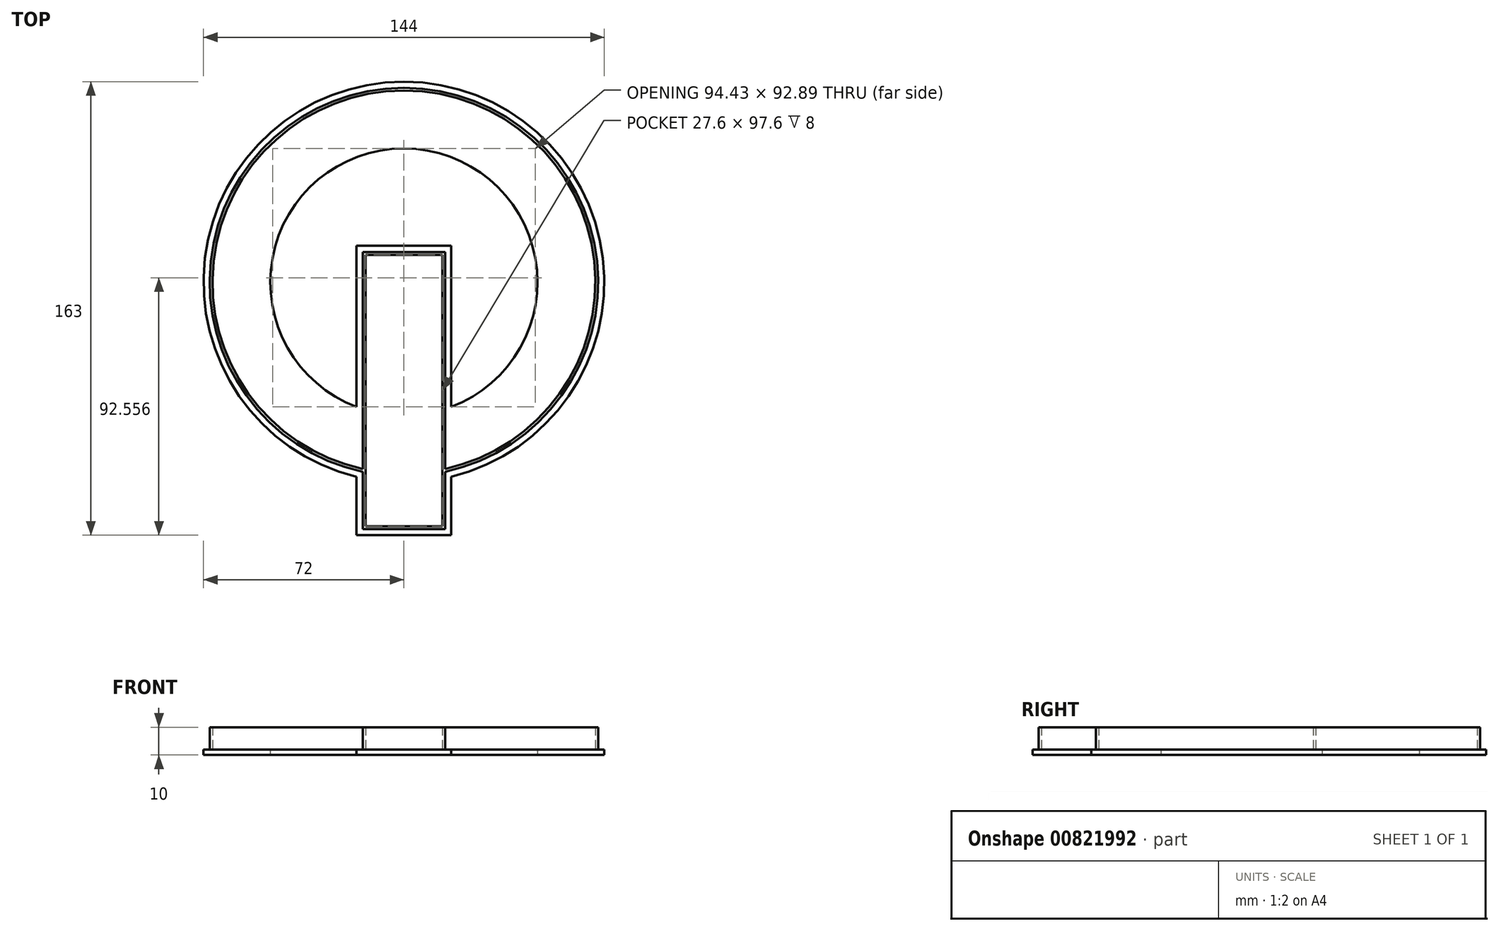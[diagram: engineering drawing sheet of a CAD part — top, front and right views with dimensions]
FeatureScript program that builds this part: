
annotation { "Feature Type Name" : "Feature", "Feature Type Description" : "" }
export const myFeature = defineFeature(function(context is Context, id is Id, definition is map)
    precondition{}
    {
        {
            var Q0;
            Q0=qCreatedBy(makeId("Top.planeOp"),FACE);
            var sketch = newSketch(context, id + "F0", { "sketchPlane" : qUnion([Q0])});
            skCircle(sketch, "E0", {"center": v(0, 0) * mm, "radius": 69.8 * mm});
            skCircle(sketch, "E1", {"center": v(0, 0) * mm, "radius": 68.8 * mm});
            skSolve(sketch);
        }
        {
            var Q0;
            Q0=makeQuery(id+"F0.imprint","IMPRINT",FACE,{"disambiguationData":[TD([[makeQuery(id+"F0.imprint","IMPRINT",EDGE,{"derivedFrom":sQuery(id+"F0.wireOp",EDGE,"E0")}),1.0]])]});
            extrude(context, id + "F1", {"entities" : qUnion([Q0]), "depth" : 10 * mm, "offsetDistance" : 25 * mm});
        }
        {
            var Q0;
            Q0=qCreatedBy(makeId("Top.planeOp"),FACE);
            var sketch = newSketch(context, id + "F2", { "sketchPlane" : qUnion([Q0])});
            skLineSegment(sketch, "E2.bottom", {"start": v(-14.8, 10.8) * mm, "end": v(14.8, 10.8) * mm});
            skLineSegment(sketch, "E2.top", {"start": v(-14.8, -88.8) * mm, "end": v(14.8, -88.8) * mm});
            skLineSegment(sketch, "E2.left", {"start": v(-14.8, 10.8) * mm, "end": v(-14.8, -88.8) * mm});
            skLineSegment(sketch, "E2.right", {"start": v(14.8, 10.8) * mm, "end": v(14.8, -88.8) * mm});
            skPoint(sketch, "E2.middle", {"position": v(0, -39) * mm});
            skLineSegment(sketch, "E3.bottom", {"start": v(-13.8, 9.8) * mm, "end": v(13.8, 9.8) * mm});
            skLineSegment(sketch, "E3.top", {"start": v(-13.8, -87.8) * mm, "end": v(13.8, -87.8) * mm});
            skLineSegment(sketch, "E3.left", {"start": v(-13.8, 9.8) * mm, "end": v(-13.8, -87.8) * mm});
            skLineSegment(sketch, "E3.right", {"start": v(13.8, 9.8) * mm, "end": v(13.8, -87.8) * mm});
            skSolve(sketch);
        }
        {
            var Q0;
            Q0=makeQuery(id+"F2.imprint","IMPRINT",FACE,{"disambiguationData":[TD([[makeQuery(id+"F2.imprint","IMPRINT",EDGE,{"derivedFrom":sQuery(id+"F2.wireOp",EDGE,"E2.bottom")}),-1.0]])]});
            extrude(context, id + "F3", {"entities" : qUnion([Q0]), "operationType" : NewBodyOperationType.ADD, "depth" : 10 * mm, "offsetDistance" : 25 * mm});
        }
        {
            var Q0;
            Q0=qCreatedBy(makeId("Top.planeOp"),FACE);
            var sketch = newSketch(context, id + "F4", { "sketchPlane" : qUnion([Q0])});
            skCircle(sketch, "E4", {"center": v(0, 0) * mm, "radius": 48 * mm});
            skCircle(sketch, "E5", {"center": v(0, 0) * mm, "radius": 68.8 * mm});
            skSolve(sketch);
        }
        {
            var Q0;
            Q0=makeQuery(id+"F4.imprint","IMPRINT",FACE,{"disambiguationData":[TD([[makeQuery(id+"F4.imprint","IMPRINT",EDGE,{"derivedFrom":sQuery(id+"F4.wireOp",EDGE,"E4")}),-1.0]])]});
            extrude(context, id + "F5", {"entities" : qUnion([Q0]), "operationType" : NewBodyOperationType.ADD, "depth" : 2 * mm, "offsetDistance" : 25 * mm});
        }
        {
            var Q0;
            Q0=qCreatedBy(makeId("Top.planeOp"),FACE);
            var sketch = newSketch(context, id + "F6", { "sketchPlane" : qUnion([Q0])});
            skCircle(sketch, "E6", {"center": v(0, 0) * mm, "radius": 69.8 * mm});
            skCircle(sketch, "E7", {"center": v(0, 0) * mm, "radius": 72 * mm});
            skSolve(sketch);
        }
        {
            var Q0;
            Q0=makeQuery(id+"F6.imprint","IMPRINT",FACE,{"disambiguationData":[TD([[makeQuery(id+"F6.imprint","IMPRINT",EDGE,{"derivedFrom":sQuery(id+"F6.wireOp",EDGE,"E6")}),-1.0]])]});
            extrude(context, id + "F7", {"entities" : qUnion([Q0]), "operationType" : NewBodyOperationType.ADD, "depth" : 2 * mm, "offsetDistance" : 25 * mm});
        }
        {
            var Q0;
            Q0=qCreatedBy(makeId("Top.planeOp"),FACE);
            var sketch = newSketch(context, id + "F8", { "sketchPlane" : qUnion([Q0])});
            skLineSegment(sketch, "E8.bottom", {"start": v(-14.8, 10.8) * mm, "end": v(14.8, 10.8) * mm});
            skLineSegment(sketch, "E8.top", {"start": v(-14.8, -88.8) * mm, "end": v(14.8, -88.8) * mm});
            skLineSegment(sketch, "E8.left", {"start": v(-14.8, 10.8) * mm, "end": v(-14.8, -88.8) * mm});
            skLineSegment(sketch, "E8.right", {"start": v(14.8, 10.8) * mm, "end": v(14.8, -88.8) * mm});
            skPoint(sketch, "E8.middle", {"position": v(0, -39) * mm});
            skLineSegment(sketch, "E9.bottom", {"start": v(-17, 13) * mm, "end": v(17, 13) * mm});
            skLineSegment(sketch, "E9.top", {"start": v(-17, -91) * mm, "end": v(17, -91) * mm});
            skLineSegment(sketch, "E9.left", {"start": v(-17, 13) * mm, "end": v(-17, -91) * mm});
            skLineSegment(sketch, "E9.right", {"start": v(17, 13) * mm, "end": v(17, -91) * mm});
            skSolve(sketch);
        }
        {
            var Q0;
            Q0=makeQuery(id+"F8.imprint","IMPRINT",FACE,{"disambiguationData":[TD([[makeQuery(id+"F8.imprint","IMPRINT",EDGE,{"derivedFrom":sQuery(id+"F8.wireOp",EDGE,"E8.bottom")}),1.0]])]});
            extrude(context, id + "F9", {"entities" : qUnion([Q0]), "operationType" : NewBodyOperationType.ADD, "depth" : 2 * mm, "offsetDistance" : 25 * mm});
        }
        {
            var Q0;
            Q0=qCreatedBy(makeId("Top.planeOp"),FACE);
            var sketch = newSketch(context, id + "F10", { "sketchPlane" : qUnion([Q0])});
            skLineSegment(sketch, "E10.bottom", {"start": v(-13.8, 9.8) * mm, "end": v(13.8, 9.8) * mm});
            skLineSegment(sketch, "E10.top", {"start": v(-13.8, -87.8) * mm, "end": v(13.8, -87.8) * mm});
            skLineSegment(sketch, "E10.left", {"start": v(-13.8, 9.8) * mm, "end": v(-13.8, -87.8) * mm});
            skLineSegment(sketch, "E10.right", {"start": v(13.8, 9.8) * mm, "end": v(13.8, -87.8) * mm});
            skPoint(sketch, "E10.middle", {"position": v(0, -39) * mm});
            skSolve(sketch);
        }
        {
            var Q0;
            Q0=makeQuery(id+"F10.imprint","IMPRINT",FACE,{"disambiguationData":[TD([[makeQuery(id+"F10.imprint","IMPRINT",EDGE,{"derivedFrom":sQuery(id+"F10.wireOp",EDGE,"E10.bottom")}),-1.0]])]});
            extrude(context, id + "F11", {"entities" : qUnion([Q0]), "operationType" : NewBodyOperationType.ADD, "depth" : 2 * mm, "offsetDistance" : 25 * mm});
        }
        {
            var Q0;
            Q0=qCreatedBy(makeId("Front.planeOp"),FACE);
            var sketch = newSketch(context, id + "F12", { "sketchPlane" : qUnion([Q0])});
            skLineSegment(sketch, "E11.bottom", {"start": v(-13.8, 10) * mm, "end": v(13.8, 10) * mm});
            skLineSegment(sketch, "E11.top", {"start": v(-13.8, 2) * mm, "end": v(13.8, 2) * mm});
            skLineSegment(sketch, "E11.left", {"start": v(-13.8, 10) * mm, "end": v(-13.8, 2) * mm});
            skLineSegment(sketch, "E11.right", {"start": v(13.8, 10) * mm, "end": v(13.8, 2) * mm});
            skPoint(sketch, "E11.middle", {"position": v(0, 6) * mm});
            skSolve(sketch);
        }
        {
            var Q0;
            Q0=makeQuery(id+"F12.imprint","IMPRINT",FACE,{"disambiguationData":[TD([[makeQuery(id+"F12.imprint","IMPRINT",EDGE,{"derivedFrom":sQuery(id+"F12.wireOp",EDGE,"E11.bottom")}),-1.0]])]});
            extrude(context, id + "F13", {"entities" : qUnion([Q0]), "operationType" : NewBodyOperationType.REMOVE, "depth" : 70 * mm, "offsetDistance" : 25 * mm});
        }
    });
